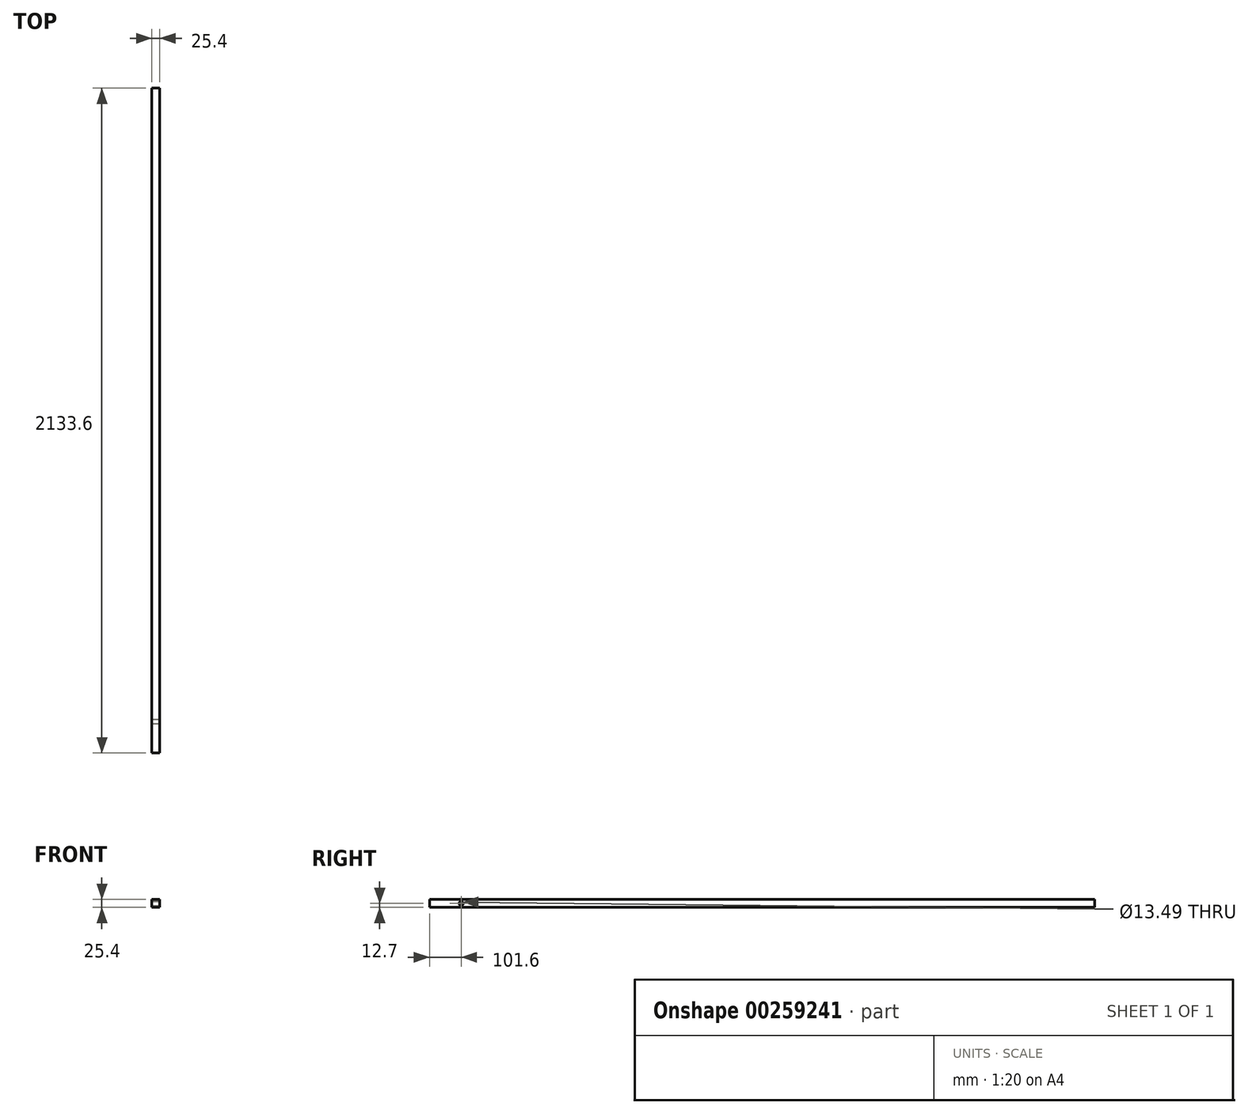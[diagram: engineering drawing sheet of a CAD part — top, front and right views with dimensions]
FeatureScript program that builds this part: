
annotation { "Feature Type Name" : "Feature", "Feature Type Description" : "" }
export const myFeature = defineFeature(function(context is Context, id is Id, definition is map)
    precondition{}
    {
        {
            var Q0;
            Q0=qCreatedBy(makeId("Front.planeOp"),FACE);
            var sketch = newSketch(context, id + "F0", { "sketchPlane" : qUnion([Q0])});
            skLineSegment(sketch, "E0.bottom", {"start": v(-20.6, -6.35) * mm, "end": v(4.8, -6.35) * mm});
            skLineSegment(sketch, "E0.top", {"start": v(-20.6, 19.05) * mm, "end": v(4.8, 19.05) * mm});
            skLineSegment(sketch, "E0.left", {"start": v(-20.6, -6.35) * mm, "end": v(-20.6, 19.05) * mm});
            skLineSegment(sketch, "E0.right", {"start": v(4.8, -6.35) * mm, "end": v(4.8, 19.05) * mm});
            skSolve(sketch);
        }
        {
            var Q0;
            Q0=makeQuery(id+"F0.imprint","IMPRINT",FACE,{"disambiguationData":[TD([[makeQuery(id+"F0.imprint","IMPRINT",EDGE,{"derivedFrom":sQuery(id+"F0.wireOp",EDGE,"E0.bottom")}),1.0]])]});
            extrude(context, id + "F1", {"entities" : qUnion([Q0]), "depth" : 2133.6 * mm});
        }
        {
            var Q0;
            Q0=makeQuery(id+"F1.opExtrude","SWEPT_FACE",FACE,{"disambiguationData":[OSD([sQuery(id+"F0.wireOp",EDGE,"E0.right")])]});
            var sketch = newSketch(context, id + "F2", { "sketchPlane" : qUnion([Q0])});
            skLineSegment(sketch, "E1", {"start": v(-2133.6, 6.35) * mm, "end": v(-2032, 6.35) * mm});
            skCircle(sketch, "E2", {"center": v(-2032, 6.35) * mm, "radius": 6.35 * mm});
            skSolve(sketch);
        }
        {
            var Q0;
            Q0=sQuery(id+"F2.wireOp",VERTEX,"E2.center");
            var Q1;
            Q1=makeQuery(id+"F1.opExtrude","SWEPT_BODY",BODY,{"disambiguationData":[OSD([sQuery(id+"F0.wireOp",EDGE,"E0.bottom"),sQuery(id+"F0.wireOp",EDGE,"E0.top"),sQuery(id+"F0.wireOp",EDGE,"E0.left"),sQuery(id+"F0.wireOp",EDGE,"E0.right")])]});
            hole(context, id + "F3", {"style" : HoleStyle.SIMPLE, "endStyle" : HoleEndStyle.THROUGH, "standardTappedOrClearance" : lookupTablePath({ "standard" : "ANSI", "fit" : "Normal (ASME)", "size" : "1/2", "type" : "Clearance" }), "standardBlindInLast" : lookupTablePath({ "fit" : "Free", "standard" : "ANSI", "size" : "1/2", "type" : "Clearance" }), "holeDiameter" : 13.5 * mm, "tappedDepth" : 12.7 * mm, "tapClearance" : 3, "locations" : qUnion([Q0]), "scope" : qUnion([Q1])});
        }
    });
